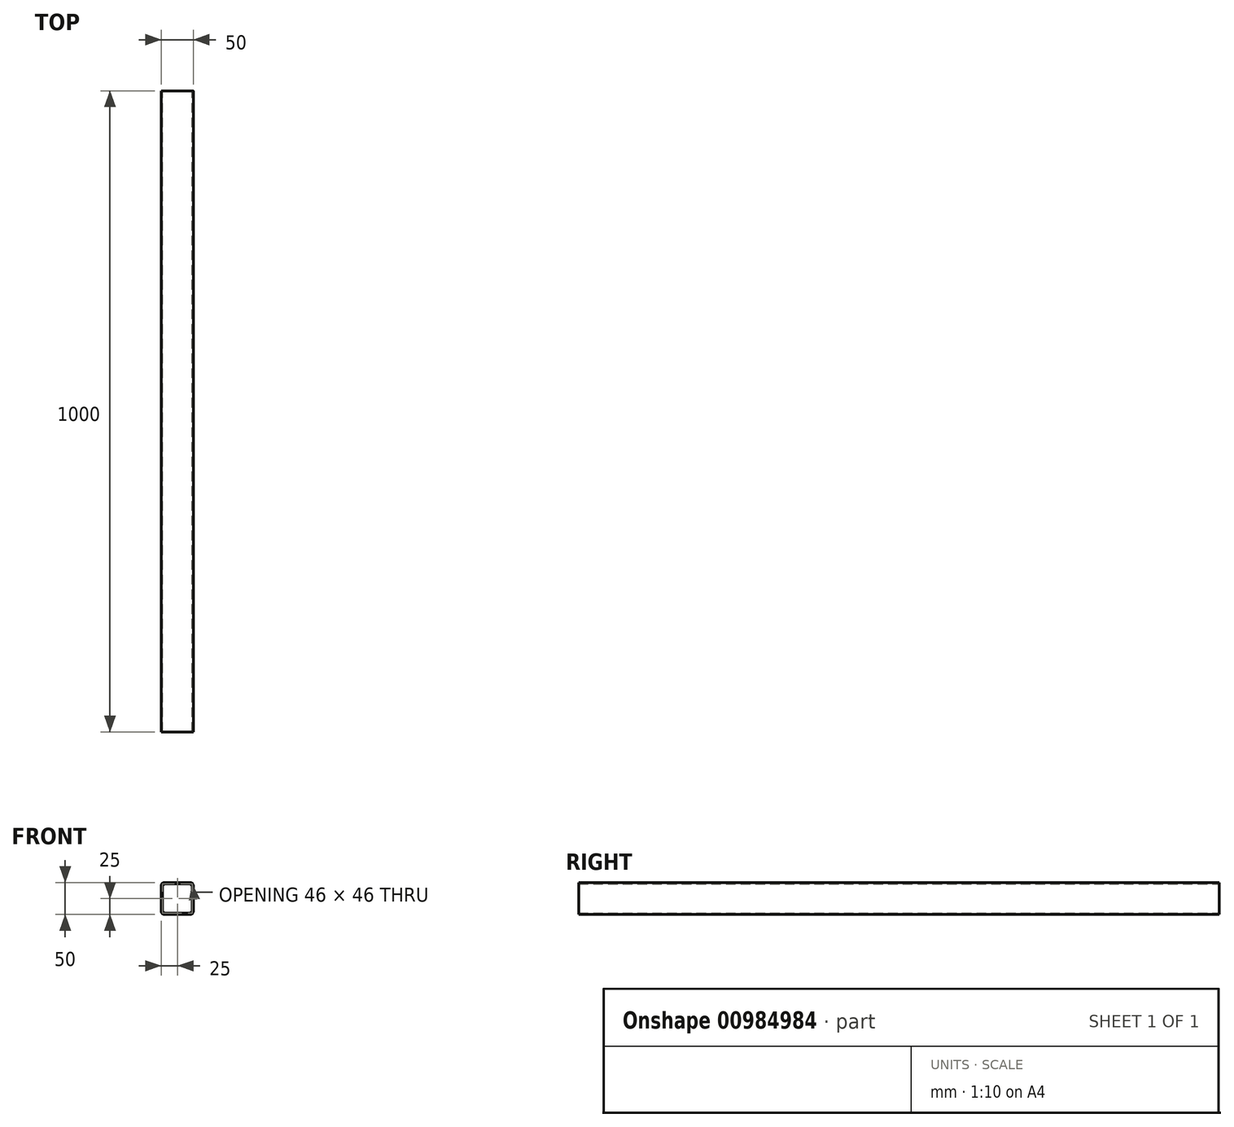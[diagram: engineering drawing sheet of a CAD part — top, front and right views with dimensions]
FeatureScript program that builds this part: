
annotation { "Feature Type Name" : "Feature", "Feature Type Description" : "" }
export const myFeature = defineFeature(function(context is Context, id is Id, definition is map)
    precondition{}
    {
        {
            var Q0;
            Q0=qCreatedBy(makeId("Front.planeOp"),FACE);
            var sketch = newSketch(context, id + "F0", { "sketchPlane" : qUnion([Q0])});
            skLineSegment(sketch, "E0.bottom", {"start": v(-20, 25) * mm, "end": v(20, 25) * mm});
            skLineSegment(sketch, "E0.top", {"start": v(-20, -25) * mm, "end": v(20, -25) * mm});
            skLineSegment(sketch, "E0.left", {"start": v(-25, 20) * mm, "end": v(-25, -20) * mm});
            skLineSegment(sketch, "E0.right", {"start": v(25, 20) * mm, "end": v(25, -20) * mm});
            skLineSegment(sketch, "E1.0", {"start": v(23, 18) * mm, "end": v(23, -18) * mm});
            skLineSegment(sketch, "E1.1", {"start": v(-18, 23) * mm, "end": v(18, 23) * mm});
            skLineSegment(sketch, "E1.2", {"start": v(-23, 18) * mm, "end": v(-23, -18) * mm});
            skLineSegment(sketch, "E1.3", {"start": v(-18, -23) * mm, "end": v(18, -23) * mm});
            skPoint(sketch, "E2.visualSharp", {"position": v(25, 25) * mm});
            skArc(sketch, "E2.filletArc", {"start": v(25, 20) * mm, "mid": v(23.54, 23.54) * mm, "end": v(20, 25) * mm});
            skPoint(sketch, "E3.visualSharp", {"position": v(23, 23) * mm});
            skArc(sketch, "E3.filletArc", {"start": v(23, 18) * mm, "mid": v(21.54, 21.54) * mm, "end": v(18, 23) * mm});
            skPoint(sketch, "E4.visualSharp", {"position": v(-23, -23) * mm});
            skArc(sketch, "E4.filletArc", {"start": v(-23, -18) * mm, "mid": v(-21.54, -21.54) * mm, "end": v(-18, -23) * mm});
            skPoint(sketch, "E5.visualSharp", {"position": v(-25, -25) * mm});
            skArc(sketch, "E5.filletArc", {"start": v(-25, -20) * mm, "mid": v(-23.54, -23.54) * mm, "end": v(-20, -25) * mm});
            skPoint(sketch, "E6.visualSharp", {"position": v(-23, 23) * mm});
            skArc(sketch, "E6.filletArc", {"start": v(-18, 23) * mm, "mid": v(-21.54, 21.54) * mm, "end": v(-23, 18) * mm});
            skPoint(sketch, "E7.visualSharp", {"position": v(-25, 25) * mm});
            skArc(sketch, "E7.filletArc", {"start": v(-20, 25) * mm, "mid": v(-23.54, 23.54) * mm, "end": v(-25, 20) * mm});
            skPoint(sketch, "E8.visualSharp", {"position": v(23, -23) * mm});
            skArc(sketch, "E8.filletArc", {"start": v(18, -23) * mm, "mid": v(21.54, -21.54) * mm, "end": v(23, -18) * mm});
            skPoint(sketch, "E9.visualSharp", {"position": v(25, -25) * mm});
            skArc(sketch, "E9.filletArc", {"start": v(20, -25) * mm, "mid": v(23.54, -23.54) * mm, "end": v(25, -20) * mm});
            skSolve(sketch);
        }
        {
            var Q0;
            Q0=makeQuery(id+"F0.imprint","IMPRINT",FACE,{"disambiguationData":[TD([[makeQuery(id+"F0.imprint","IMPRINT",EDGE,{"derivedFrom":sQuery(id+"F0.wireOp",EDGE,"E0.bottom")}),-1.0]])]});
            extrude(context, id + "F1", {"entities" : qUnion([Q0]), "depth" : 1000 * mm, "offsetDistance" : 25.4 * mm});
        }
    });
